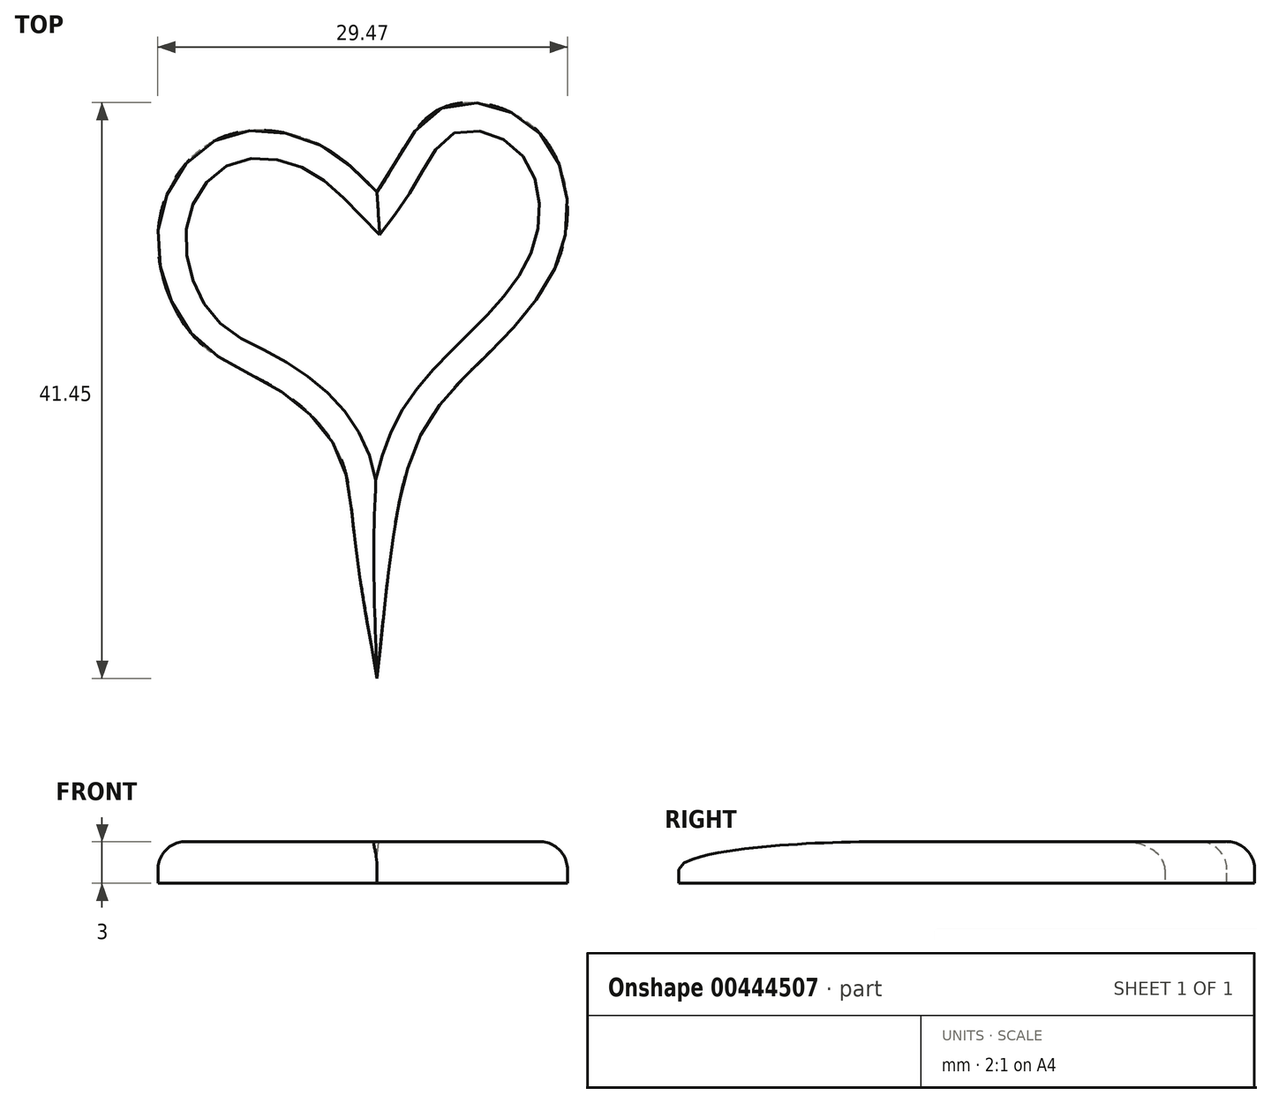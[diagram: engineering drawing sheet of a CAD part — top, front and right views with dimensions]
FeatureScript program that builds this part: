
annotation { "Feature Type Name" : "Feature", "Feature Type Description" : "" }
export const myFeature = defineFeature(function(context is Context, id is Id, definition is map)
    precondition{}
    {
        {
            var Q0;
            Q0=qCreatedBy(makeId("Top.planeOp"),FACE);
            var sketch = newSketch(context, id + "F0", { "sketchPlane" : qUnion([Q0])});
            skFitSpline(sketch, "E0", {"points": [v(0, 10.47) * mm, v(4.43, 16.41) * mm, v(11.6, 14.84) * mm, v(13.1, 5.72) * mm, v(6.28, -2.85) * mm, v(2.28, -9.13) * mm, v(0, -24.53) * mm], "startDerivative": vector(29.53, 39.5) * mm, "endDerivative": vector(-7.67, -68.6) * mm});
            skFitSpline(sketch, "E1", {"points": [v(0, 10.47) * mm, v(-4.43, 14.02) * mm, v(-11.25, 14.39) * mm, v(-15.68, 8.3) * mm, v(-13.1, 0) * mm, v(-7.2, -3.69) * mm, v(-2.77, -8.3) * mm, v(-1.66, -14.02) * mm, v(0, -24.53) * mm], "startDerivative": vector(-35.22, 36.46) * mm, "endDerivative": vector(13.2, -74.38) * mm});
            skSolve(sketch);
        }
        {
            var Q0;
            Q0 = qSketchRegion(id + "F0", true);
            extrude(context, id + "F1", {"entities" : qUnion([Q0]), "depth" : 3 * mm});
        }
        {
            var Q0;
            Q0=makeQuery(id+"F1.opExtrude","CAP_EDGE",EDGE,{"disambiguationData":[OSD([sQuery(id+"F0.wireOp",EDGE,"E1")])],"isStart":false});
            var Q1;
            Q1=makeQuery(id+"F1.opExtrude","CAP_EDGE",EDGE,{"disambiguationData":[OSD([sQuery(id+"F0.wireOp",EDGE,"E0")])],"isStart":false});
            fillet(context, id + "F2", {"entities" : qUnion([Q0, Q1]), "radius" : 2 * mm, "tangentPropagation" : true, "allowEdgeOverflow" : false});
        }
    });
